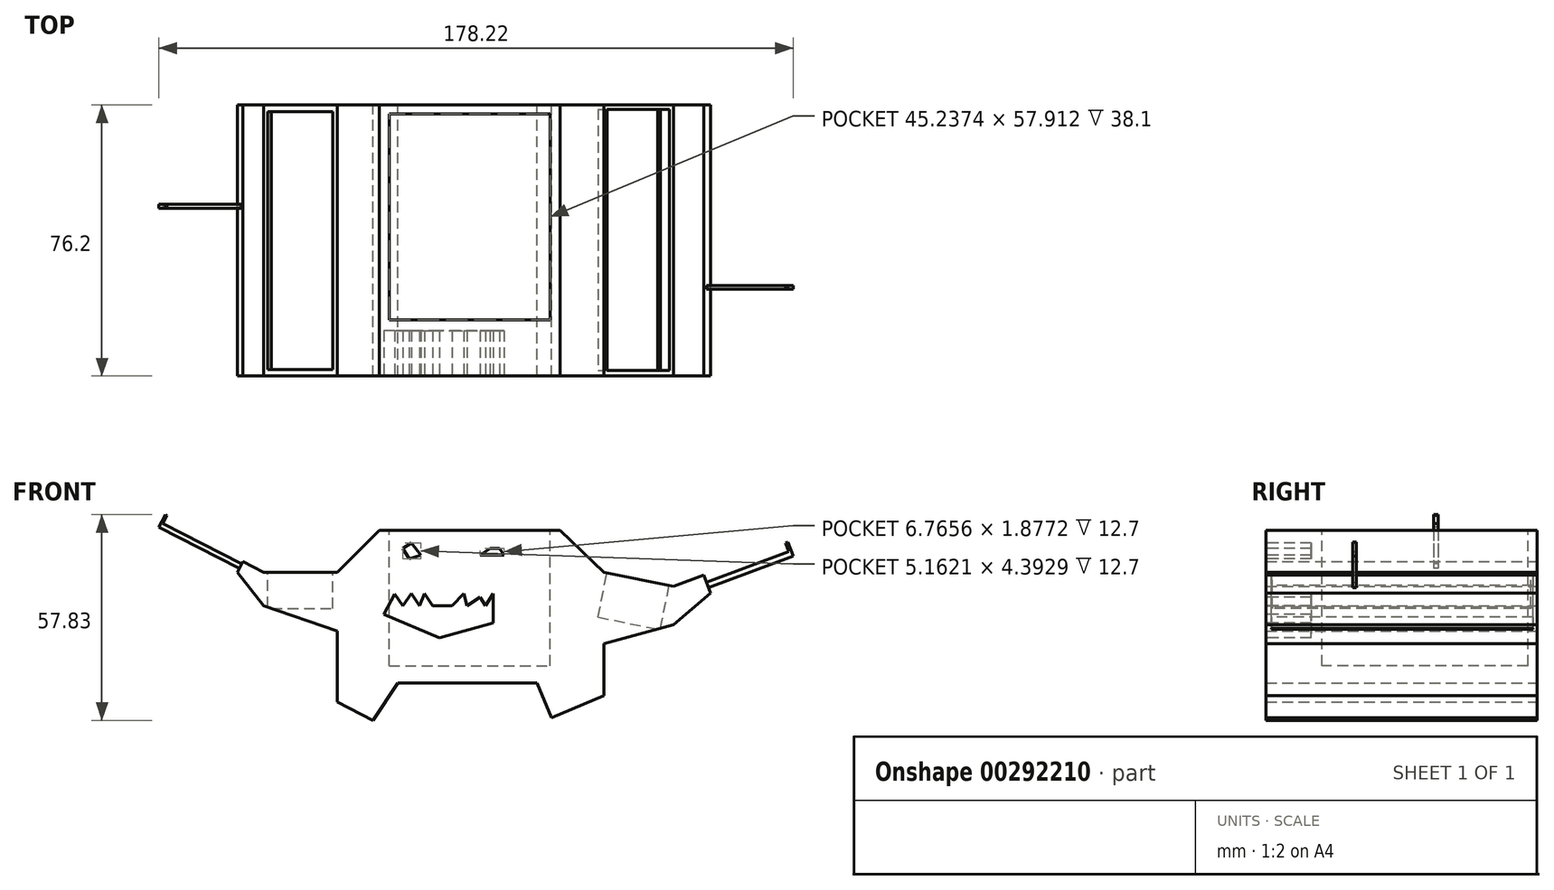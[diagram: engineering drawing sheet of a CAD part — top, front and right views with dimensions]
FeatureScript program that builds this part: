
annotation { "Feature Type Name" : "Feature", "Feature Type Description" : "" }
export const myFeature = defineFeature(function(context is Context, id is Id, definition is map)
    precondition{}
    {
        {
            var Q0;
            Q0=qCreatedBy(makeId("Front.planeOp"),FACE);
            var sketch = newSketch(context, id + "F0", { "sketchPlane" : qUnion([Q0])});
            skLineSegment(sketch, "E0", {"start": v(-41.93, 56.14) * mm, "end": v(8.87, 56.14) * mm});
            skLineSegment(sketch, "E1", {"start": v(8.87, 56.14) * mm, "end": v(21.21, 44.3) * mm});
            skLineSegment(sketch, "E2", {"start": v(21.21, 44.3) * mm, "end": v(40.74, 40.35) * mm});
            skLineSegment(sketch, "E3", {"start": v(40.74, 40.35) * mm, "end": v(49.23, 43.5) * mm});
            skLineSegment(sketch, "E4", {"start": v(49.23, 43.5) * mm, "end": v(51.12, 38.42) * mm});
            skLineSegment(sketch, "E5", {"start": v(51.12, 38.42) * mm, "end": v(40.74, 29.5) * mm});
            skLineSegment(sketch, "E6", {"start": v(40.74, 29.5) * mm, "end": v(21.21, 24.17) * mm});
            skLineSegment(sketch, "E7", {"start": v(21.21, 24.17) * mm, "end": v(21.21, 9.57) * mm});
            skLineSegment(sketch, "E8", {"start": v(21.21, 9.57) * mm, "end": v(6.41, 3.45) * mm});
            skLineSegment(sketch, "E9", {"start": v(-41.93, 56.14) * mm, "end": v(-53.77, 44.3) * mm});
            skLineSegment(sketch, "E10", {"start": v(-53.77, 44.3) * mm, "end": v(-74.49, 44.3) * mm});
            skLineSegment(sketch, "E11", {"start": v(-74.49, 44.3) * mm, "end": v(-80.3, 47.28) * mm});
            skLineSegment(sketch, "E12", {"start": v(-80.3, 47.28) * mm, "end": v(-81.84, 44.3) * mm});
            skLineSegment(sketch, "E13", {"start": v(-81.84, 44.3) * mm, "end": v(-74.49, 34.9) * mm});
            skLineSegment(sketch, "E14", {"start": v(-74.49, 34.9) * mm, "end": v(-53.77, 27.72) * mm});
            skLineSegment(sketch, "E15", {"start": v(-53.77, 27.72) * mm, "end": v(-53.77, 7.8) * mm});
            skLineSegment(sketch, "E16", {"start": v(-53.77, 7.8) * mm, "end": v(-43.7, 2.66) * mm});
            skLineSegment(sketch, "E17", {"start": v(6.41, 3.45) * mm, "end": v(2.42, 13.11) * mm});
            skLineSegment(sketch, "E18", {"start": v(2.42, 13.11) * mm, "end": v(-36.8, 13.11) * mm});
            skLineSegment(sketch, "E19", {"start": v(-36.8, 13.11) * mm, "end": v(-43.7, 2.66) * mm});
            skSolve(sketch);
        }
        {
            var Q0;
            Q0=makeQuery(id+"F0.imprint","IMPRINT",FACE,{"disambiguationData":[TD([[makeQuery(id+"F0.imprint","IMPRINT",EDGE,{"derivedFrom":sQuery(id+"F0.wireOp",EDGE,"E0")}),-1.0]])]});
            extrude(context, id + "F1", {"entities" : qUnion([Q0]), "depth" : 76.2 * mm});
        }
        {
            var Q0;
            Q0=makeQuery(id+"F1.opExtrude","SWEPT_FACE",FACE,{"disambiguationData":[OSD([sQuery(id+"F0.wireOp",EDGE,"E0")])]});
            var sketch = newSketch(context, id + "F2", { "sketchPlane" : qUnion([Q0])});
            skLineSegment(sketch, "E20.bottom", {"start": v(-39.2, -2.54) * mm, "end": v(6.03, -2.54) * mm});
            skLineSegment(sketch, "E20.top", {"start": v(-39.2, -60.45) * mm, "end": v(6.03, -60.45) * mm});
            skLineSegment(sketch, "E20.left", {"start": v(-39.2, -2.54) * mm, "end": v(-39.2, -60.45) * mm});
            skLineSegment(sketch, "E20.right", {"start": v(6.03, -2.54) * mm, "end": v(6.03, -60.45) * mm});
            skSolve(sketch);
        }
        {
            var Q0;
            Q0=makeQuery(id+"F2.imprint","IMPRINT",FACE,{"disambiguationData":[TD([[makeQuery(id+"F2.imprint","IMPRINT",EDGE,{"derivedFrom":sQuery(id+"F2.wireOp",EDGE,"E20.bottom")}),-1.0]])]});
            extrude(context, id + "F3", {"entities" : qUnion([Q0]), "operationType" : NewBodyOperationType.REMOVE, "oppositeDirection" : true, "depth" : 38.1 * mm});
        }
        {
            var Q0;
            Q0=makeQuery(id+"F1.opExtrude","SWEPT_FACE",FACE,{"disambiguationData":[OSD([sQuery(id+"F0.wireOp",EDGE,"E4")])]});
            var sketch = newSketch(context, id + "F4", { "sketchPlane" : qUnion([Q0])});
            skLineSegment(sketch, "E21.bottom", {"start": v(-73.24, 22.23) * mm, "end": v(-72.25, 22.23) * mm});
            skLineSegment(sketch, "E21.top", {"start": v(-73.24, 20.63) * mm, "end": v(-72.25, 20.63) * mm});
            skLineSegment(sketch, "E21.left", {"start": v(-73.24, 22.23) * mm, "end": v(-73.24, 20.63) * mm});
            skLineSegment(sketch, "E21.right", {"start": v(-72.25, 22.23) * mm, "end": v(-72.25, 20.63) * mm});
            skLineSegment(sketch, "E22.bottom", {"start": v(-51.76, 21.47) * mm, "end": v(-50.77, 21.47) * mm});
            skLineSegment(sketch, "E22.top", {"start": v(-51.76, 19.87) * mm, "end": v(-50.77, 19.87) * mm});
            skLineSegment(sketch, "E22.left", {"start": v(-51.76, 21.47) * mm, "end": v(-51.76, 19.87) * mm});
            skLineSegment(sketch, "E22.right", {"start": v(-50.77, 21.47) * mm, "end": v(-50.77, 19.87) * mm});
            skLineSegment(sketch, "E23.bottom", {"start": v(-26.72, 21.47) * mm, "end": v(-25.73, 21.47) * mm});
            skLineSegment(sketch, "E23.top", {"start": v(-26.72, 19.87) * mm, "end": v(-25.73, 19.87) * mm});
            skLineSegment(sketch, "E23.left", {"start": v(-26.72, 21.47) * mm, "end": v(-26.72, 19.87) * mm});
            skLineSegment(sketch, "E23.right", {"start": v(-25.73, 21.47) * mm, "end": v(-25.73, 19.87) * mm});
            skSolve(sketch);
        }
        {
            var Q0;
            Q0=makeQuery(id+"F4.imprint","IMPRINT",FACE,{"disambiguationData":[TD([[makeQuery(id+"F4.imprint","IMPRINT",EDGE,{"derivedFrom":sQuery(id+"F4.wireOp",EDGE,"E22.bottom")}),-1.0]])]});
            extrude(context, id + "F5", {"entities" : qUnion([Q0]), "operationType" : NewBodyOperationType.ADD, "depth" : 25.4 * mm});
        }
        {
            var Q0;
            Q0=makeQuery(id+"F5.opExtrude","SWEPT_FACE",FACE,{"disambiguationData":[OSD([sQuery(id+"F4.wireOp",EDGE,"E22.bottom")])]});
            var sketch = newSketch(context, id + "F6", { "sketchPlane" : qUnion([Q0])});
            skLineSegment(sketch, "E24.bottom", {"start": v(86.71, -51.76) * mm, "end": v(85.98, -51.76) * mm});
            skLineSegment(sketch, "E24.top", {"start": v(86.71, -50.77) * mm, "end": v(85.98, -50.77) * mm});
            skLineSegment(sketch, "E24.left", {"start": v(86.71, -51.76) * mm, "end": v(86.71, -50.77) * mm});
            skLineSegment(sketch, "E24.right", {"start": v(85.98, -51.76) * mm, "end": v(85.98, -50.77) * mm});
            skSolve(sketch);
        }
        {
            var Q0;
            Q0=makeQuery(id+"F6.imprint","IMPRINT",FACE,{"disambiguationData":[TD([[makeQuery(id+"F6.imprint","IMPRINT",EDGE,{"derivedFrom":sQuery(id+"F6.wireOp",EDGE,"E24.bottom")}),-1.0]])]});
            extrude(context, id + "F7", {"entities" : qUnion([Q0]), "operationType" : NewBodyOperationType.ADD, "depth" : 2.54 * mm});
        }
        {
            var Q0;
            Q0=makeQuery(id+"F1.opExtrude","SWEPT_FACE",FACE,{"disambiguationData":[OSD([sQuery(id+"F0.wireOp",EDGE,"E12")])]});
            var sketch = newSketch(context, id + "F8", { "sketchPlane" : qUnion([Q0])});
            skLineSegment(sketch, "E25.bottom", {"start": v(27.86, 4.7) * mm, "end": v(29.04, 4.7) * mm});
            skLineSegment(sketch, "E25.top", {"start": v(27.86, 3.3) * mm, "end": v(29.04, 3.3) * mm});
            skLineSegment(sketch, "E25.left", {"start": v(27.86, 4.7) * mm, "end": v(27.86, 3.3) * mm});
            skLineSegment(sketch, "E25.right", {"start": v(29.04, 4.7) * mm, "end": v(29.04, 3.3) * mm});
            skSolve(sketch);
        }
        {
            var Q0;
            Q0=makeQuery(id+"F8.imprint","IMPRINT",FACE,{"disambiguationData":[TD([[makeQuery(id+"F8.imprint","IMPRINT",EDGE,{"derivedFrom":sQuery(id+"F8.wireOp",EDGE,"E25.bottom")}),-1.0]])]});
            extrude(context, id + "F9", {"entities" : qUnion([Q0]), "operationType" : NewBodyOperationType.ADD, "depth" : 25.4 * mm});
        }
        {
            var Q0;
            Q0=makeQuery(id+"F9.opExtrude","SWEPT_FACE",FACE,{"disambiguationData":[OSD([sQuery(id+"F8.wireOp",EDGE,"E25.bottom")])]});
            var sketch = newSketch(context, id + "F10", { "sketchPlane" : qUnion([Q0])});
            skLineSegment(sketch, "E26.bottom", {"start": v(-118.43, -27.86) * mm, "end": v(-117.9, -27.86) * mm});
            skLineSegment(sketch, "E26.top", {"start": v(-118.43, -29.04) * mm, "end": v(-117.9, -29.04) * mm});
            skLineSegment(sketch, "E26.left", {"start": v(-118.43, -27.86) * mm, "end": v(-118.43, -29.04) * mm});
            skLineSegment(sketch, "E26.right", {"start": v(-117.9, -27.86) * mm, "end": v(-117.9, -29.04) * mm});
            skSolve(sketch);
        }
        {
            var Q0;
            Q0=makeQuery(id+"F10.imprint","IMPRINT",FACE,{"disambiguationData":[TD([[makeQuery(id+"F10.imprint","IMPRINT",EDGE,{"derivedFrom":sQuery(id+"F10.wireOp",EDGE,"E26.bottom")}),-1.0]])]});
            extrude(context, id + "F11", {"entities" : qUnion([Q0]), "operationType" : NewBodyOperationType.ADD, "depth" : 2.54 * mm});
        }
        {
            var Q0;
            Q0=makeQuery(id+"F1.opExtrude","CAP_FACE",FACE,{"disambiguationData":[OSD([sQuery(id+"F0.wireOp",EDGE,"E0"),sQuery(id+"F0.wireOp",EDGE,"E1"),sQuery(id+"F0.wireOp",EDGE,"E2"),sQuery(id+"F0.wireOp",EDGE,"E3"),sQuery(id+"F0.wireOp",EDGE,"E4"),sQuery(id+"F0.wireOp",EDGE,"E5"),sQuery(id+"F0.wireOp",EDGE,"E6"),sQuery(id+"F0.wireOp",EDGE,"E7"),sQuery(id+"F0.wireOp",EDGE,"E8"),sQuery(id+"F0.wireOp",EDGE,"E9"),sQuery(id+"F0.wireOp",EDGE,"E10"),sQuery(id+"F0.wireOp",EDGE,"E11"),sQuery(id+"F0.wireOp",EDGE,"E12"),sQuery(id+"F0.wireOp",EDGE,"E13"),sQuery(id+"F0.wireOp",EDGE,"E14"),sQuery(id+"F0.wireOp",EDGE,"E15"),sQuery(id+"F0.wireOp",EDGE,"E16"),sQuery(id+"F0.wireOp",EDGE,"E17"),sQuery(id+"F0.wireOp",EDGE,"E18"),sQuery(id+"F0.wireOp",EDGE,"E19")])],"isStart":false});
            var sketch = newSketch(context, id + "F12", { "sketchPlane" : qUnion([Q0])});
            skLineSegment(sketch, "E27", {"start": v(-32.94, 52.55) * mm, "end": v(-35.4, 51.02) * mm});
            skLineSegment(sketch, "E28", {"start": v(-35.4, 51.02) * mm, "end": v(-33.63, 48.15) * mm});
            skLineSegment(sketch, "E29", {"start": v(-33.63, 48.15) * mm, "end": v(-30.24, 49.14) * mm});
            skLineSegment(sketch, "E30", {"start": v(-30.24, 49.14) * mm, "end": v(-32.94, 52.55) * mm});
            skLineSegment(sketch, "E31", {"start": v(-10.88, 51.02) * mm, "end": v(-13.7, 49.14) * mm});
            skLineSegment(sketch, "E32", {"start": v(-10.88, 51.02) * mm, "end": v(-8.18, 51.02) * mm});
            skLineSegment(sketch, "E33", {"start": v(-8.18, 51.02) * mm, "end": v(-6.93, 49.14) * mm});
            skLineSegment(sketch, "E34", {"start": v(-6.93, 49.14) * mm, "end": v(-13.7, 49.14) * mm});
            skLineSegment(sketch, "E35", {"start": v(-37.63, 38.23) * mm, "end": v(-35.4, 34.89) * mm});
            skLineSegment(sketch, "E36", {"start": v(-35.4, 34.89) * mm, "end": v(-32.94, 38.35) * mm});
            skLineSegment(sketch, "E37", {"start": v(-32.94, 38.35) * mm, "end": v(-30.63, 34.89) * mm});
            skLineSegment(sketch, "E38", {"start": v(-30.63, 34.89) * mm, "end": v(-29.3, 38.35) * mm});
            skLineSegment(sketch, "E39", {"start": v(-29.3, 38.35) * mm, "end": v(-27, 34.89) * mm});
            skLineSegment(sketch, "E40", {"start": v(-27, 34.89) * mm, "end": v(-21.56, 34.89) * mm});
            skLineSegment(sketch, "E41", {"start": v(-21.56, 34.89) * mm, "end": v(-18.27, 38.35) * mm});
            skLineSegment(sketch, "E42", {"start": v(-18.27, 38.35) * mm, "end": v(-17.34, 34.89) * mm});
            skLineSegment(sketch, "E43", {"start": v(-17.34, 34.89) * mm, "end": v(-13.7, 37.31) * mm});
            skLineSegment(sketch, "E44", {"start": v(-13.7, 37.31) * mm, "end": v(-12.08, 34.89) * mm});
            skLineSegment(sketch, "E45", {"start": v(-12.08, 34.89) * mm, "end": v(-9.94, 38.35) * mm});
            skLineSegment(sketch, "E46", {"start": v(-9.94, 38.35) * mm, "end": v(-9.94, 30.02) * mm});
            skLineSegment(sketch, "E47", {"start": v(-9.94, 30.02) * mm, "end": v(-25.08, 25.91) * mm});
            skLineSegment(sketch, "E48", {"start": v(-25.08, 25.91) * mm, "end": v(-40.68, 32.48) * mm});
            skLineSegment(sketch, "E49", {"start": v(-37.63, 38.23) * mm, "end": v(-40.68, 32.48) * mm});
            skSolve(sketch);
        }
        {
            var Q0;
            Q0=makeQuery(id+"F12.imprint","IMPRINT",FACE,{"disambiguationData":[TD([[makeQuery(id+"F12.imprint","IMPRINT",EDGE,{"derivedFrom":sQuery(id+"F12.wireOp",EDGE,"E35")}),-1.0]])]});
            var Q1;
            Q1=makeQuery(id+"F12.imprint","IMPRINT",FACE,{"disambiguationData":[TD([[makeQuery(id+"F12.imprint","IMPRINT",EDGE,{"derivedFrom":sQuery(id+"F12.wireOp",EDGE,"E27")}),1.0]])]});
            var Q2;
            Q2=makeQuery(id+"F12.imprint","IMPRINT",FACE,{"disambiguationData":[TD([[makeQuery(id+"F12.imprint","IMPRINT",EDGE,{"derivedFrom":sQuery(id+"F12.wireOp",EDGE,"E31")}),1.0]])]});
            extrude(context, id + "F13", {"entities" : qUnion([Q0, Q1, Q2]), "operationType" : NewBodyOperationType.REMOVE, "oppositeDirection" : true, "depth" : 12.7 * mm});
        }
        {
            var Q0;
            Q0=makeQuery(id+"F1.opExtrude","SWEPT_FACE",FACE,{"disambiguationData":[OSD([sQuery(id+"F0.wireOp",EDGE,"E2")])]});
            var sketch = newSketch(context, id + "F14", { "sketchPlane" : qUnion([Q0])});
            skLineSegment(sketch, "E50.bottom", {"start": v(12.87, -1.17) * mm, "end": v(30.7, -1.17) * mm});
            skLineSegment(sketch, "E50.top", {"start": v(12.87, -74.65) * mm, "end": v(30.7, -74.65) * mm});
            skLineSegment(sketch, "E50.left", {"start": v(12.87, -1.17) * mm, "end": v(12.87, -74.65) * mm});
            skLineSegment(sketch, "E50.right", {"start": v(30.7, -1.17) * mm, "end": v(30.7, -74.65) * mm});
            skSolve(sketch);
        }
        {
            var Q0;
            Q0=makeQuery(id+"F14.imprint","IMPRINT",FACE,{"disambiguationData":[TD([[makeQuery(id+"F14.imprint","IMPRINT",EDGE,{"derivedFrom":sQuery(id+"F14.wireOp",EDGE,"E50.bottom")}),-1.0]])]});
            extrude(context, id + "F15", {"entities" : qUnion([Q0]), "operationType" : NewBodyOperationType.REMOVE, "oppositeDirection" : true, "depth" : 12.7 * mm});
        }
        {
            var Q0;
            Q0=makeQuery(id+"F1.opExtrude","SWEPT_FACE",FACE,{"disambiguationData":[OSD([sQuery(id+"F0.wireOp",EDGE,"E10")])]});
            var sketch = newSketch(context, id + "F16", { "sketchPlane" : qUnion([Q0])});
            skLineSegment(sketch, "E51.bottom", {"start": v(-73.3, -1.84) * mm, "end": v(-55.05, -1.84) * mm});
            skLineSegment(sketch, "E51.top", {"start": v(-73.3, -74.42) * mm, "end": v(-55.05, -74.42) * mm});
            skLineSegment(sketch, "E51.left", {"start": v(-73.3, -1.84) * mm, "end": v(-73.3, -74.42) * mm});
            skLineSegment(sketch, "E51.right", {"start": v(-55.05, -1.84) * mm, "end": v(-55.05, -74.42) * mm});
            skSolve(sketch);
        }
        {
            var Q0;
            Q0=makeQuery(id+"F16.imprint","IMPRINT",FACE,{"disambiguationData":[TD([[makeQuery(id+"F16.imprint","IMPRINT",EDGE,{"derivedFrom":sQuery(id+"F16.wireOp",EDGE,"E51.bottom")}),-1.0]])]});
            extrude(context, id + "F17", {"entities" : qUnion([Q0]), "operationType" : NewBodyOperationType.REMOVE, "oppositeDirection" : true, "depth" : 10.16 * mm});
        }
    });
